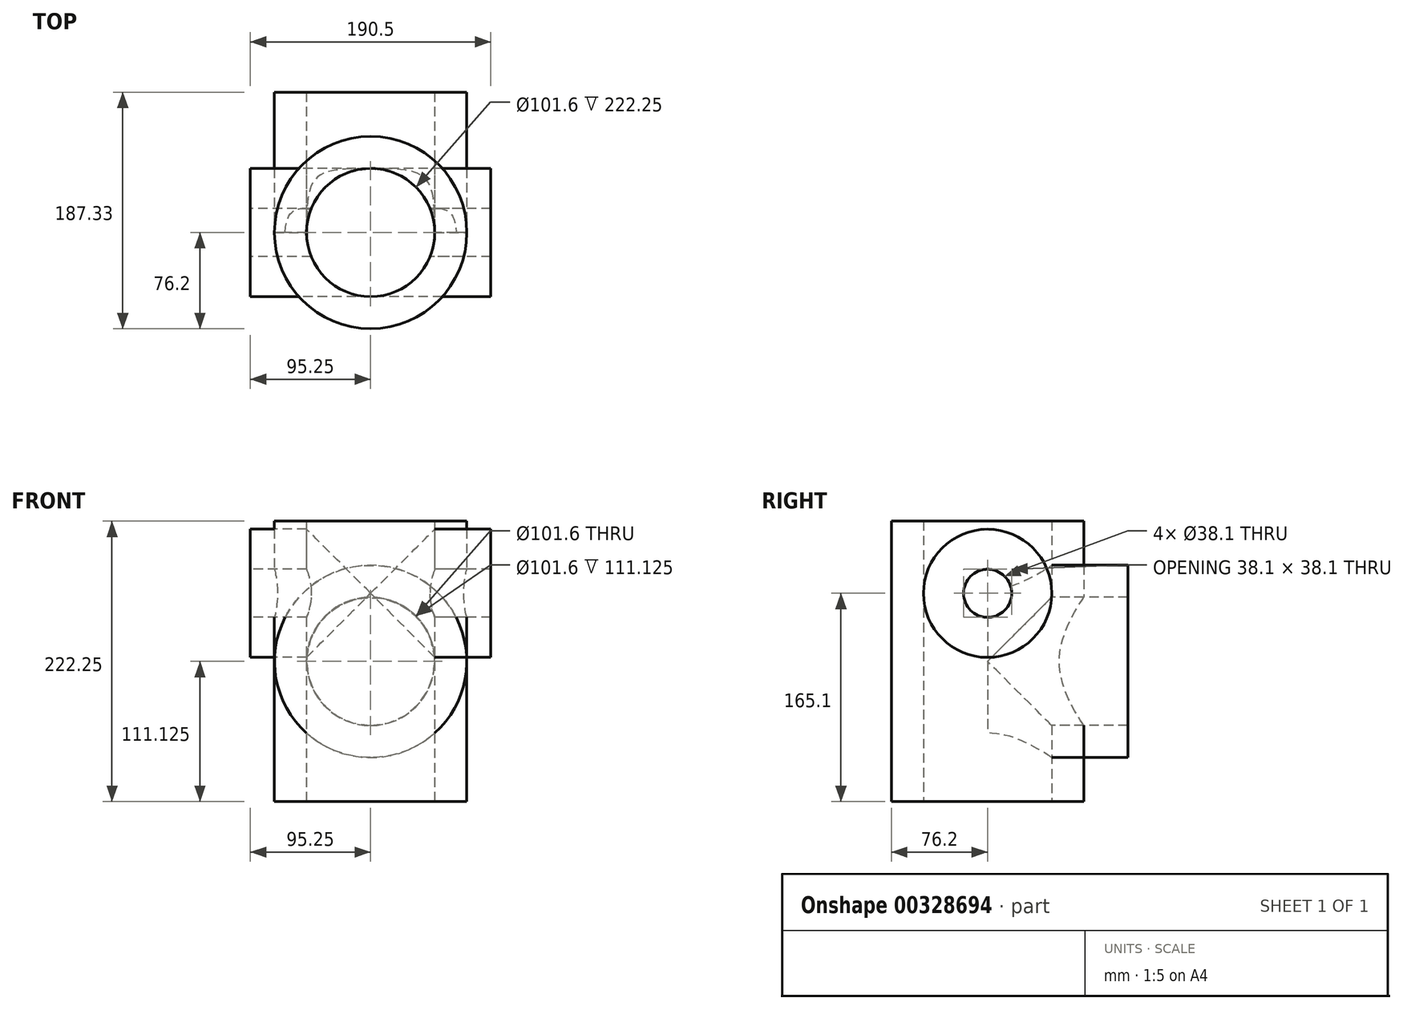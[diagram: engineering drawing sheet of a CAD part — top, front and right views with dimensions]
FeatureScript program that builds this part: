
annotation { "Feature Type Name" : "Feature", "Feature Type Description" : "" }
export const myFeature = defineFeature(function(context is Context, id is Id, definition is map)
    precondition{}
    {
        {
            var Q0;
            Q0=qCreatedBy(makeId("Top.planeOp"),FACE);
            var sketch = newSketch(context, id + "F0", { "sketchPlane" : qUnion([Q0])});
            skCircle(sketch, "E0", {"center": v(0, 0) * mm, "radius": 50.8 * mm});
            skSolve(sketch);
        }
        {
            var Q0;
            Q0 = qSketchRegion(id + "F0", true);
            extrude(context, id + "F1", {"entities" : qUnion([Q0]), "depth" : 222.25 * mm});
        }
        {
            var Q0;
            Q0=qCreatedBy(makeId("Right.planeOp"),FACE);
            var sketch = newSketch(context, id + "F2", { "sketchPlane" : qUnion([Q0])});
            skCircle(sketch, "E1", {"center": v(0, 165.1) * mm, "radius": 19.05 * mm});
            skSolve(sketch);
        }
        {
            var Q0;
            Q0 = qSketchRegion(id + "F2", true);
            extrude(context, id + "F3", {"entities" : qUnion([Q0]), "operationType" : NewBodyOperationType.ADD, "endBound" : BoundingType.SYMMETRIC, "depth" : 190.5 * mm});
        }
        {
            var Q0;
            Q0=qCreatedBy(makeId("Front.planeOp"),FACE);
            var sketch = newSketch(context, id + "F4", { "sketchPlane" : qUnion([Q0])});
            skCircle(sketch, "E2", {"center": v(0, 165.1) * mm, "radius": 19.05 * mm});
            skSolve(sketch);
        }
        {
            var Q0;
            Q0 = qSketchRegion(id + "F4", true);
            extrude(context, id + "F5", {"entities" : qUnion([Q0]), "operationType" : NewBodyOperationType.ADD, "depth" : 7.5 / 50.8 * mm});
        }
        {
            var Q0;
            Q0=qCreatedBy(makeId("Front.planeOp"),FACE);
            var sketch = newSketch(context, id + "F6", { "sketchPlane" : qUnion([Q0])});
            skCircle(sketch, "E3", {"center": v(0, 111.13) * mm, "radius": 50.8 * mm});
            skSolve(sketch);
        }
        {
            var Q0;
            Q0 = qSketchRegion(id + "F6", true);
            extrude(context, id + "F7", {"entities" : qUnion([Q0]), "operationType" : NewBodyOperationType.ADD, "depth" : -111.12 * mm});
        }
        {
            var Q0;
            Q0=qCreatedBy(makeId("Top.planeOp"),FACE);
            var sketch = newSketch(context, id + "F8", { "sketchPlane" : qUnion([Q0])});
            skCircle(sketch, "E4", {"center": v(0, 0) * mm, "radius": 76.2 * mm});
            skSolve(sketch);
        }
        {
            var Q0;
            Q0 = qSketchRegion(id + "F8", true);
            extrude(context, id + "F9", {"entities" : qUnion([Q0]), "depth" : 222.25 * mm});
        }
        {
            var Q0;
            Q0=qCreatedBy(makeId("Right.planeOp"),FACE);
            var sketch = newSketch(context, id + "F10", { "sketchPlane" : qUnion([Q0])});
            skCircle(sketch, "E5", {"center": v(0, 165.1) * mm, "radius": 50.8 * mm});
            skSolve(sketch);
        }
        {
            var Q0;
            Q0 = qSketchRegion(id + "F10", true);
            extrude(context, id + "F11", {"entities" : qUnion([Q0]), "endBound" : BoundingType.SYMMETRIC, "depth" : 190.5 * mm});
        }
        {
            var Q0;
            Q0=qCreatedBy(makeId("Front.planeOp"),FACE);
            var sketch = newSketch(context, id + "F12", { "sketchPlane" : qUnion([Q0])});
            skCircle(sketch, "E6", {"center": v(0, 165.1) * mm, "radius": 50.8 * mm});
            skSolve(sketch);
        }
        {
            var Q0;
            Q0 = qSketchRegion(id + "F12", true);
            extrude(context, id + "F13", {"entities" : qUnion([Q0]), "depth" : 7.5 / 50.8 * mm});
        }
        {
            var Q0;
            Q0=qCreatedBy(makeId("Front.planeOp"),FACE);
            var sketch = newSketch(context, id + "F14", { "sketchPlane" : qUnion([Q0])});
            skCircle(sketch, "E7", {"center": v(0, 111.13) * mm, "radius": 76.2 * mm});
            skSolve(sketch);
        }
        {
            var Q0;
            Q0 = qSketchRegion(id + "F14", true);
            extrude(context, id + "F15", {"entities" : qUnion([Q0]), "depth" : -111.12 * mm});
        }
        {
            var Q0;
            Q0=makeQuery(id+"F1.opExtrude","SWEPT_BODY",BODY,{"disambiguationData":[OSD([sQuery(id+"F0.wireOp",EDGE,"E0")])]});
            var Q1;
            Q1=makeQuery(id+"F9.opExtrude","SWEPT_BODY",BODY,{"disambiguationData":[OSD([sQuery(id+"F8.wireOp",EDGE,"E4")])]});
            var Q2;
            Q2=makeQuery(id+"F13.opExtrude","SWEPT_BODY",BODY,{"disambiguationData":[OSD([sQuery(id+"F12.wireOp",EDGE,"E6")])]});
            var Q3;
            Q3=makeQuery(id+"F15.opExtrude","SWEPT_BODY",BODY,{"disambiguationData":[OSD([sQuery(id+"F14.wireOp",EDGE,"E7")])]});
            var Q4;
            Q4=makeQuery(id+"F11.opExtrude","SWEPT_BODY",BODY,{"disambiguationData":[OSD([sQuery(id+"F10.wireOp",EDGE,"E5")])]});
            booleanBodies(context, id + "F16", {"operationType" : BooleanOperationType.SUBTRACTION, "tools" : qUnion([Q0]), "targets" : qUnion([Q1, Q2, Q3, Q4])});
        }
    });
